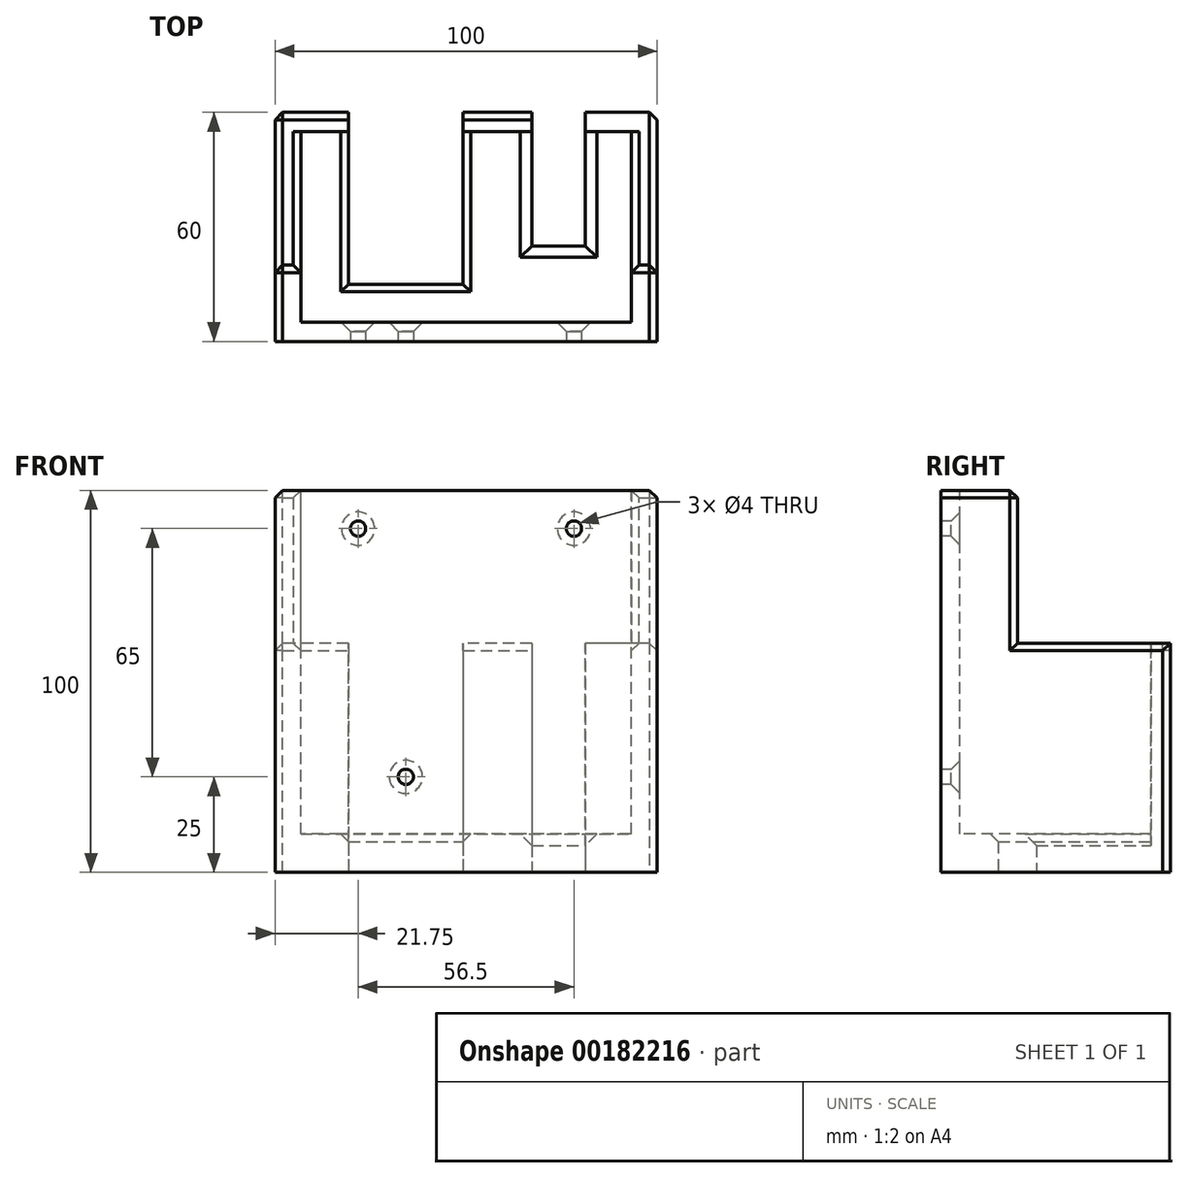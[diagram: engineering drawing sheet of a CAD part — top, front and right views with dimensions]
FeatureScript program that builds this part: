
annotation { "Feature Type Name" : "Feature", "Feature Type Description" : "" }
export const myFeature = defineFeature(function(context is Context, id is Id, definition is map)
    precondition{}
    {
        {
            var Q0;
            Q0=qCreatedBy(makeId("Right.planeOp"),FACE);
            var sketch = newSketch(context, id + "F0", { "sketchPlane" : qUnion([Q0])});
            skLineSegment(sketch, "E0", {"start": v(0, 0) * mm, "end": v(-60, 0) * mm});
            skLineSegment(sketch, "E1", {"start": v(-60, 0) * mm, "end": v(-60, 100) * mm});
            skLineSegment(sketch, "E2", {"start": v(-60, 100) * mm, "end": v(-40, 100) * mm});
            skLineSegment(sketch, "E3", {"start": v(-40, 100) * mm, "end": v(-40, 60) * mm});
            skLineSegment(sketch, "E4", {"start": v(-40, 60) * mm, "end": v(0, 60) * mm});
            skLineSegment(sketch, "E5", {"start": v(0, 60) * mm, "end": v(0, 0) * mm});
            skSolve(sketch);
        }
        {
            var Q0;
            Q0 = qSketchRegion(id + "F0", true);
            var Q1;
            Q1=makeQuery(id+"F0.imprint","IMPRINT",FACE,{"disambiguationData":[TD([[makeQuery(id+"F0.imprint","IMPRINT",EDGE,{"derivedFrom":sQuery(id+"F0.wireOp",EDGE,"E0")}),-1.0]])]});
            extrude(context, id + "F1", {"entities" : qUnion([Q0, Q1]), "depth" : 100 * mm});
        }
        {
            var Q0;
            Q0=makeQuery(id+"F1.opExtrude","SWEPT_FACE",FACE,{"disambiguationData":[OSD([sQuery(id+"F0.wireOp",EDGE,"E2")])]});
            var sketch = newSketch(context, id + "F2", { "sketchPlane" : qUnion([Q0])});
            skLineSegment(sketch, "E6", {"start": v(0, -60) * mm, "end": v(6.75, -60) * mm});
            skLineSegment(sketch, "E7", {"start": v(6.75, -60) * mm, "end": v(6.75, -55) * mm});
            skLineSegment(sketch, "E8", {"start": v(6.75, -55) * mm, "end": v(93.25, -55) * mm});
            skLineSegment(sketch, "E9", {"start": v(93.25, -55) * mm, "end": v(93.25, -5) * mm});
            skLineSegment(sketch, "E10", {"start": v(93.25, -5) * mm, "end": v(6.75, -5) * mm});
            skLineSegment(sketch, "E11", {"start": v(6.75, -5) * mm, "end": v(6.75, -55) * mm});
            skSolve(sketch);
        }
        {
            var Q0;
            Q0 = qSketchRegion(id + "F2", true);
            extrude(context, id + "F3", {"entities" : qUnion([Q0]), "operationType" : NewBodyOperationType.REMOVE, "oppositeDirection" : true, "depth" : 90 * mm});
        }
        {
            var Q0;
            Q0=makeQuery(id+"F1.opExtrude","SWEPT_FACE",FACE,{"disambiguationData":[OSD([sQuery(id+"F0.wireOp",EDGE,"E0")])]});
            var sketch = newSketch(context, id + "F4", { "sketchPlane" : qUnion([Q0])});
            skLineSegment(sketch, "E12", {"start": v(0, 0) * mm, "end": v(6.75, 0) * mm});
            skLineSegment(sketch, "E13", {"start": v(6.75, 0) * mm, "end": v(19.25, 0) * mm});
            skLineSegment(sketch, "E14", {"start": v(19.25, 0) * mm, "end": v(49.25, 0) * mm});
            skLineSegment(sketch, "E15", {"start": v(49.25, 0) * mm, "end": v(49.25, 45) * mm});
            skLineSegment(sketch, "E16", {"start": v(49.25, 45) * mm, "end": v(19.25, 45) * mm});
            skLineSegment(sketch, "E17", {"start": v(19.25, 45) * mm, "end": v(19.25, 0) * mm});
            skLineSegment(sketch, "E18", {"start": v(100, 0) * mm, "end": v(93.25, 0) * mm});
            skLineSegment(sketch, "E19", {"start": v(93.25, 0) * mm, "end": v(81.25, 0) * mm});
            skLineSegment(sketch, "E20", {"start": v(81.25, 0) * mm, "end": v(67.25, 0) * mm});
            skLineSegment(sketch, "E21", {"start": v(67.25, 0) * mm, "end": v(67.25, 35) * mm});
            skLineSegment(sketch, "E22", {"start": v(67.25, 35) * mm, "end": v(81.25, 35) * mm});
            skLineSegment(sketch, "E23", {"start": v(81.25, 35) * mm, "end": v(81.25, 0) * mm});
            skLineSegment(sketch, "E24", {"start": v(67.25, 0) * mm, "end": v(67.25, 10) * mm});
            skLineSegment(sketch, "E25", {"start": v(67.25, 10) * mm, "end": v(81.25, 10) * mm});
            skSolve(sketch);
        }
        {
            var Q0;
            Q0=makeQuery(id+"F4.imprint","IMPRINT",FACE,{"disambiguationData":[TD([[makeQuery(id+"F4.imprint","IMPRINT",EDGE,{"derivedFrom":sQuery(id+"F4.wireOp",EDGE,"E14")}),-1.0]])]});
            var Q1;
            Q1=makeQuery(id+"F4.imprint","IMPRINT",FACE,{"disambiguationData":[TD([[makeQuery(id+"F4.imprint","IMPRINT",EDGE,{"derivedFrom":sQuery(id+"F4.wireOp",EDGE,"E21")}),-1.0]])]});
            var Q2;
            Q2=makeQuery(id+"F4.imprint","IMPRINT",FACE,{"disambiguationData":[TD([[makeQuery(id+"F4.imprint","IMPRINT",EDGE,{"derivedFrom":sQuery(id+"F4.wireOp",EDGE,"E14")}),-1.0]])]});
            extrude(context, id + "F5", {"entities" : qUnion([Q0, Q1, Q2]), "operationType" : NewBodyOperationType.REMOVE, "oppositeDirection" : true, "depth" : 60 * mm});
        }
        {
            var Q0;
            Q0=makeQuery(id+"F3.boolean.opBoolean","COPY",FACE,{"derivedFrom":makeQuery(id+"F3.opExtrude","SWEPT_FACE",FACE,{"disambiguationData":[OSD([sQuery(id+"F2.wireOp",EDGE,"E8")])]})});
            var sketch = newSketch(context, id + "F6", { "sketchPlane" : qUnion([Q0])});
            skLineSegment(sketch, "E26", {"start": v(-93.25, 100) * mm, "end": v(-78.25, 100) * mm});
            skLineSegment(sketch, "E27", {"start": v(-78.25, 100) * mm, "end": v(-78.25, 90) * mm});
            skLineSegment(sketch, "E28", {"start": v(-6.75, 100) * mm, "end": v(-21.75, 100) * mm});
            skLineSegment(sketch, "E29", {"start": v(-21.75, 100) * mm, "end": v(-21.75, 90) * mm});
            skLineSegment(sketch, "E30", {"start": v(-21.75, 90) * mm, "end": v(-34.25, 90) * mm});
            skLineSegment(sketch, "E31", {"start": v(-34.25, 90) * mm, "end": v(-34.25, 25) * mm});
            skSolve(sketch);
        }
        {
            var Q0;
            Q0=sQuery(id+"F6.wireOp",VERTEX,"E27.end");
            var Q1;
            Q1=sQuery(id+"F6.wireOp",VERTEX,"E30.start");
            var Q2;
            Q2=sQuery(id+"F6.wireOp",VERTEX,"E31.end");
            var Q3;
            Q3=makeQuery(id+"F1.opExtrude","SWEPT_BODY",BODY,{"disambiguationData":[OSD([sQuery(id+"F0.wireOp",EDGE,"E0"),sQuery(id+"F0.wireOp",EDGE,"E1"),sQuery(id+"F0.wireOp",EDGE,"E2"),sQuery(id+"F0.wireOp",EDGE,"E3"),sQuery(id+"F0.wireOp",EDGE,"E4"),sQuery(id+"F0.wireOp",EDGE,"E5")])]});
            hole(context, id + "F7", {"style" : HoleStyle.C_SINK, "endStyle" : HoleEndStyle.THROUGH, "holeDiameter" : 4 * mm, "cSinkDiameter" : 8.7 * mm, "cSinkAngle" : 90 * degree, "locations" : qUnion([Q0, Q1, Q2]), "scope" : qUnion([Q3]), "isTappedThrough" : true, "startStyle" : HoleStartStyle.PART});
        }
        {
            var Q0;
            {var subQ0=sQuery(id+"F0.wireOp",EDGE,"E5");var subQ1=sQuery(id+"F0.wireOp",EDGE,"E4");Q0=makeQuery(id+"F5.boolean.opBoolean","SPLIT",EDGE,{"disambiguationData":[TD([makeQuery(id+"F5.opExtrude","SWEPT_FACE",FACE,{"disambiguationData":[OSD([sQuery(id+"F4.wireOp",EDGE,"E15")])]})])],"derivedFrom":makeQuery(id+"F1.opExtrude","SWEPT_EDGE",EDGE,{"disambiguationData":[OSD([subQ1,subQ0])]})});}
            var Q1;
            Q1=makeQuery(id+"F1.opExtrude","CAP_EDGE",EDGE,{"disambiguationData":[OSD([sQuery(id+"F0.wireOp",EDGE,"E5")])],"isStart":false});
            var Q2;
            Q2=makeQuery(id+"F1.opExtrude","CAP_EDGE",EDGE,{"disambiguationData":[OSD([sQuery(id+"F0.wireOp",EDGE,"E5")])],"isStart":true});
            var Q3;
            Q3=makeQuery(id+"F5.boolean.opBoolean","COPY",EDGE,{"derivedFrom":makeQuery(id+"F5.opExtrude","SWEPT_EDGE",EDGE,{"disambiguationData":[OSD([sQuery(id+"F4.wireOp",EDGE,"E13"),sQuery(id+"F4.wireOp",EDGE,"E14"),sQuery(id+"F4.wireOp",EDGE,"E17")])]})});
            var Q4;
            Q4=makeQuery(id+"F5.boolean.opBoolean","INTERSECT",EDGE,{"derivedFrom":[makeQuery(id+"F3.boolean.opBoolean","COPY",FACE,{"derivedFrom":makeQuery(id+"F3.opExtrude","CAP_FACE",FACE,{"disambiguationData":[OSD([sQuery(id+"F2.wireOp",EDGE,"E8"),sQuery(id+"F2.wireOp",EDGE,"E9"),sQuery(id+"F2.wireOp",EDGE,"E10"),sQuery(id+"F2.wireOp",EDGE,"E11")])],"isStart":false})}),makeQuery(id+"F5.opExtrude","SWEPT_FACE",FACE,{"disambiguationData":[OSD([sQuery(id+"F4.wireOp",EDGE,"E15")])]})]});
            var Q5;
            Q5=makeQuery(id+"F5.boolean.opBoolean","INTERSECT",EDGE,{"derivedFrom":[makeQuery(id+"F3.boolean.opBoolean","COPY",FACE,{"derivedFrom":makeQuery(id+"F3.opExtrude","CAP_FACE",FACE,{"disambiguationData":[OSD([sQuery(id+"F2.wireOp",EDGE,"E8"),sQuery(id+"F2.wireOp",EDGE,"E9"),sQuery(id+"F2.wireOp",EDGE,"E10"),sQuery(id+"F2.wireOp",EDGE,"E11")])],"isStart":false})}),makeQuery(id+"F5.opExtrude","SWEPT_FACE",FACE,{"disambiguationData":[OSD([sQuery(id+"F4.wireOp",EDGE,"E16")])]})]});
            var Q6;
            Q6=makeQuery(id+"F5.boolean.opBoolean","COPY",EDGE,{"derivedFrom":makeQuery(id+"F5.opExtrude","SWEPT_EDGE",EDGE,{"disambiguationData":[OSD([sQuery(id+"F0.wireOp",EDGE,"E0"),sQuery(id+"F0.wireOp",EDGE,"E5"),sQuery(id+"F4.wireOp",EDGE,"E14"),sQuery(id+"F4.wireOp",EDGE,"E15")])]})});
            var Q7;
            Q7=makeQuery(id+"F1.opExtrude","CAP_EDGE",EDGE,{"disambiguationData":[OSD([sQuery(id+"F0.wireOp",EDGE,"E4")])],"isStart":false});
            var Q8;
            Q8=makeQuery(id+"F3.boolean.opBoolean","INTERSECT",EDGE,{"derivedFrom":[makeQuery(id+"F1.opExtrude","SWEPT_FACE",FACE,{"disambiguationData":[OSD([sQuery(id+"F0.wireOp",EDGE,"E4")])]}),makeQuery(id+"F3.opExtrude","SWEPT_FACE",FACE,{"disambiguationData":[OSD([sQuery(id+"F2.wireOp",EDGE,"E9")])]})]});
            var Q9;
            Q9=makeQuery(id+"F3.boolean.opBoolean","INTERSECT",EDGE,{"derivedFrom":[makeQuery(id+"F1.opExtrude","SWEPT_FACE",FACE,{"disambiguationData":[OSD([sQuery(id+"F0.wireOp",EDGE,"E4")])]}),makeQuery(id+"F3.opExtrude","SWEPT_FACE",FACE,{"disambiguationData":[OSD([sQuery(id+"F2.wireOp",EDGE,"E11")])]})]});
            var Q10;
            Q10=makeQuery(id+"F1.opExtrude","CAP_EDGE",EDGE,{"disambiguationData":[OSD([sQuery(id+"F0.wireOp",EDGE,"E4")])],"isStart":true});
            var Q11;
            {var subQ0=sQuery(id+"F0.wireOp",EDGE,"E5");var subQ1=sQuery(id+"F0.wireOp",EDGE,"E4");Q11=makeQuery(id+"F5.boolean.opBoolean","SPLIT",EDGE,{"disambiguationData":[TD([makeQuery(id+"F5.opExtrude","SWEPT_FACE",FACE,{"disambiguationData":[OSD([sQuery(id+"F4.wireOp",EDGE,"E17")])]})])],"derivedFrom":makeQuery(id+"F1.opExtrude","SWEPT_EDGE",EDGE,{"disambiguationData":[OSD([subQ1,subQ0])]})});}
            var Q12;
            Q12=makeQuery(id+"F1.opExtrude","CAP_EDGE",EDGE,{"disambiguationData":[OSD([sQuery(id+"F0.wireOp",EDGE,"E3")])],"isStart":true});
            var Q13;
            Q13=makeQuery(id+"F3.boolean.opBoolean","INTERSECT",EDGE,{"derivedFrom":[makeQuery(id+"F1.opExtrude","SWEPT_FACE",FACE,{"disambiguationData":[OSD([sQuery(id+"F0.wireOp",EDGE,"E3")])]}),makeQuery(id+"F3.opExtrude","SWEPT_FACE",FACE,{"disambiguationData":[OSD([sQuery(id+"F2.wireOp",EDGE,"E11")])]})]});
            var Q14;
            Q14=makeQuery(id+"F3.boolean.opBoolean","INTERSECT",EDGE,{"derivedFrom":[makeQuery(id+"F1.opExtrude","SWEPT_FACE",FACE,{"disambiguationData":[OSD([sQuery(id+"F0.wireOp",EDGE,"E3")])]}),makeQuery(id+"F3.opExtrude","SWEPT_FACE",FACE,{"disambiguationData":[OSD([sQuery(id+"F2.wireOp",EDGE,"E9")])]})]});
            var Q15;
            Q15=makeQuery(id+"F1.opExtrude","CAP_EDGE",EDGE,{"disambiguationData":[OSD([sQuery(id+"F0.wireOp",EDGE,"E3")])],"isStart":false});
            var Q16;
            {var subQ0=sQuery(id+"F0.wireOp",EDGE,"E3");var subQ1=sQuery(id+"F0.wireOp",EDGE,"E2");Q16=makeQuery(id+"F3.boolean.opBoolean","SPLIT",EDGE,{"disambiguationData":[TD([makeQuery(id+"F3.opExtrude","SWEPT_FACE",FACE,{"disambiguationData":[OSD([sQuery(id+"F2.wireOp",EDGE,"E11")])]})])],"derivedFrom":makeQuery(id+"F1.opExtrude","SWEPT_EDGE",EDGE,{"disambiguationData":[OSD([subQ1,subQ0])]})});}
            var Q17;
            Q17=makeQuery(id+"F1.opExtrude","CAP_EDGE",EDGE,{"disambiguationData":[OSD([sQuery(id+"F0.wireOp",EDGE,"E2")])],"isStart":true});
            var Q18;
            Q18=makeQuery(id+"F3.boolean.opBoolean","COPY",EDGE,{"derivedFrom":makeQuery(id+"F3.opExtrude","CAP_EDGE",EDGE,{"disambiguationData":[OSD([sQuery(id+"F2.wireOp",EDGE,"E11")])],"isStart":true})});
            var Q19;
            Q19=makeQuery(id+"F3.boolean.opBoolean","COPY",EDGE,{"derivedFrom":makeQuery(id+"F3.opExtrude","CAP_EDGE",EDGE,{"disambiguationData":[OSD([sQuery(id+"F2.wireOp",EDGE,"E9")])],"isStart":true})});
            var Q20;
            {var subQ0=sQuery(id+"F0.wireOp",EDGE,"E3");var subQ1=sQuery(id+"F0.wireOp",EDGE,"E2");Q20=makeQuery(id+"F3.boolean.opBoolean","SPLIT",EDGE,{"disambiguationData":[TD([makeQuery(id+"F3.opExtrude","SWEPT_FACE",FACE,{"disambiguationData":[OSD([sQuery(id+"F2.wireOp",EDGE,"E9")])]})])],"derivedFrom":makeQuery(id+"F1.opExtrude","SWEPT_EDGE",EDGE,{"disambiguationData":[OSD([subQ1,subQ0])]})});}
            var Q21;
            Q21=makeQuery(id+"F1.opExtrude","CAP_EDGE",EDGE,{"disambiguationData":[OSD([sQuery(id+"F0.wireOp",EDGE,"E2")])],"isStart":false});
            var Q22;
            Q22=makeQuery(id+"F3.boolean.opBoolean","COPY",EDGE,{"derivedFrom":makeQuery(id+"F3.opExtrude","CAP_EDGE",EDGE,{"disambiguationData":[OSD([sQuery(id+"F2.wireOp",EDGE,"E8")])],"isStart":true})});
            var Q23;
            Q23=makeQuery(id+"F5.boolean.opBoolean","COPY",EDGE,{"derivedFrom":makeQuery(id+"F5.opExtrude","CAP_EDGE",EDGE,{"disambiguationData":[OSD([sQuery(id+"F4.wireOp",EDGE,"E17")])],"isStart":false})});
            var Q24;
            Q24=makeQuery(id+"F5.boolean.opBoolean","COPY",EDGE,{"derivedFrom":makeQuery(id+"F5.opExtrude","CAP_EDGE",EDGE,{"disambiguationData":[OSD([sQuery(id+"F4.wireOp",EDGE,"E15")])],"isStart":false})});
            var Q25;
            Q25=makeQuery(id+"F5.boolean.opBoolean","INTERSECT",EDGE,{"derivedFrom":[makeQuery(id+"F3.boolean.opBoolean","COPY",FACE,{"derivedFrom":makeQuery(id+"F3.opExtrude","CAP_FACE",FACE,{"disambiguationData":[OSD([sQuery(id+"F2.wireOp",EDGE,"E8"),sQuery(id+"F2.wireOp",EDGE,"E9"),sQuery(id+"F2.wireOp",EDGE,"E10"),sQuery(id+"F2.wireOp",EDGE,"E11")])],"isStart":false})}),makeQuery(id+"F5.opExtrude","SWEPT_FACE",FACE,{"disambiguationData":[OSD([sQuery(id+"F4.wireOp",EDGE,"E17")])]})]});
            chamfer(context, id + "F8", {"entities" : qUnion([Q0, Q1, Q2, Q3, Q4, Q5, Q6, Q7, Q8, Q9, Q10, Q11, Q12, Q13, Q14, Q15, Q16, Q17, Q18, Q19, Q20, Q21, Q22, Q23, Q24, Q25]), "width" : 2 * mm, "tangentPropagation" : true});
        }
        {
            var Q0;
            Q0=makeQuery(id+"F5.boolean.opBoolean","INTERSECT",EDGE,{"derivedFrom":[makeQuery(id+"F3.boolean.opBoolean","COPY",FACE,{"derivedFrom":makeQuery(id+"F3.opExtrude","CAP_FACE",FACE,{"disambiguationData":[OSD([sQuery(id+"F2.wireOp",EDGE,"E8"),sQuery(id+"F2.wireOp",EDGE,"E9"),sQuery(id+"F2.wireOp",EDGE,"E10"),sQuery(id+"F2.wireOp",EDGE,"E11")])],"isStart":false})}),makeQuery(id+"F5.opExtrude","SWEPT_FACE",FACE,{"disambiguationData":[OSD([sQuery(id+"F4.wireOp",EDGE,"E21")])]})]});
            var Q1;
            Q1=makeQuery(id+"F5.boolean.opBoolean","INTERSECT",EDGE,{"derivedFrom":[makeQuery(id+"F3.boolean.opBoolean","COPY",FACE,{"derivedFrom":makeQuery(id+"F3.opExtrude","CAP_FACE",FACE,{"disambiguationData":[OSD([sQuery(id+"F2.wireOp",EDGE,"E8"),sQuery(id+"F2.wireOp",EDGE,"E9"),sQuery(id+"F2.wireOp",EDGE,"E10"),sQuery(id+"F2.wireOp",EDGE,"E11")])],"isStart":false})}),makeQuery(id+"F5.opExtrude","SWEPT_FACE",FACE,{"disambiguationData":[OSD([sQuery(id+"F4.wireOp",EDGE,"E25")])]})]});
            var Q2;
            Q2=makeQuery(id+"F5.boolean.opBoolean","INTERSECT",EDGE,{"derivedFrom":[makeQuery(id+"F3.boolean.opBoolean","COPY",FACE,{"derivedFrom":makeQuery(id+"F3.opExtrude","CAP_FACE",FACE,{"disambiguationData":[OSD([sQuery(id+"F2.wireOp",EDGE,"E8"),sQuery(id+"F2.wireOp",EDGE,"E9"),sQuery(id+"F2.wireOp",EDGE,"E10"),sQuery(id+"F2.wireOp",EDGE,"E11")])],"isStart":false})}),makeQuery(id+"F5.opExtrude","SWEPT_FACE",FACE,{"disambiguationData":[OSD([sQuery(id+"F4.wireOp",EDGE,"E23")])]})]});
            var Q3;
            Q3=makeQuery(id+"F5.boolean.opBoolean","INTERSECT",EDGE,{"derivedFrom":[makeQuery(id+"F3.boolean.opBoolean","COPY",FACE,{"derivedFrom":makeQuery(id+"F3.opExtrude","CAP_FACE",FACE,{"disambiguationData":[OSD([sQuery(id+"F2.wireOp",EDGE,"E8"),sQuery(id+"F2.wireOp",EDGE,"E9"),sQuery(id+"F2.wireOp",EDGE,"E10"),sQuery(id+"F2.wireOp",EDGE,"E11")])],"isStart":false})}),makeQuery(id+"F5.opExtrude","SWEPT_FACE",FACE,{"disambiguationData":[OSD([sQuery(id+"F4.wireOp",EDGE,"E22")])]})]});
            chamfer(context, id + "F9", {"entities" : qUnion([Q0, Q1, Q2, Q3]), "width" : 3 * mm, "tangentPropagation" : true});
        }
    });
